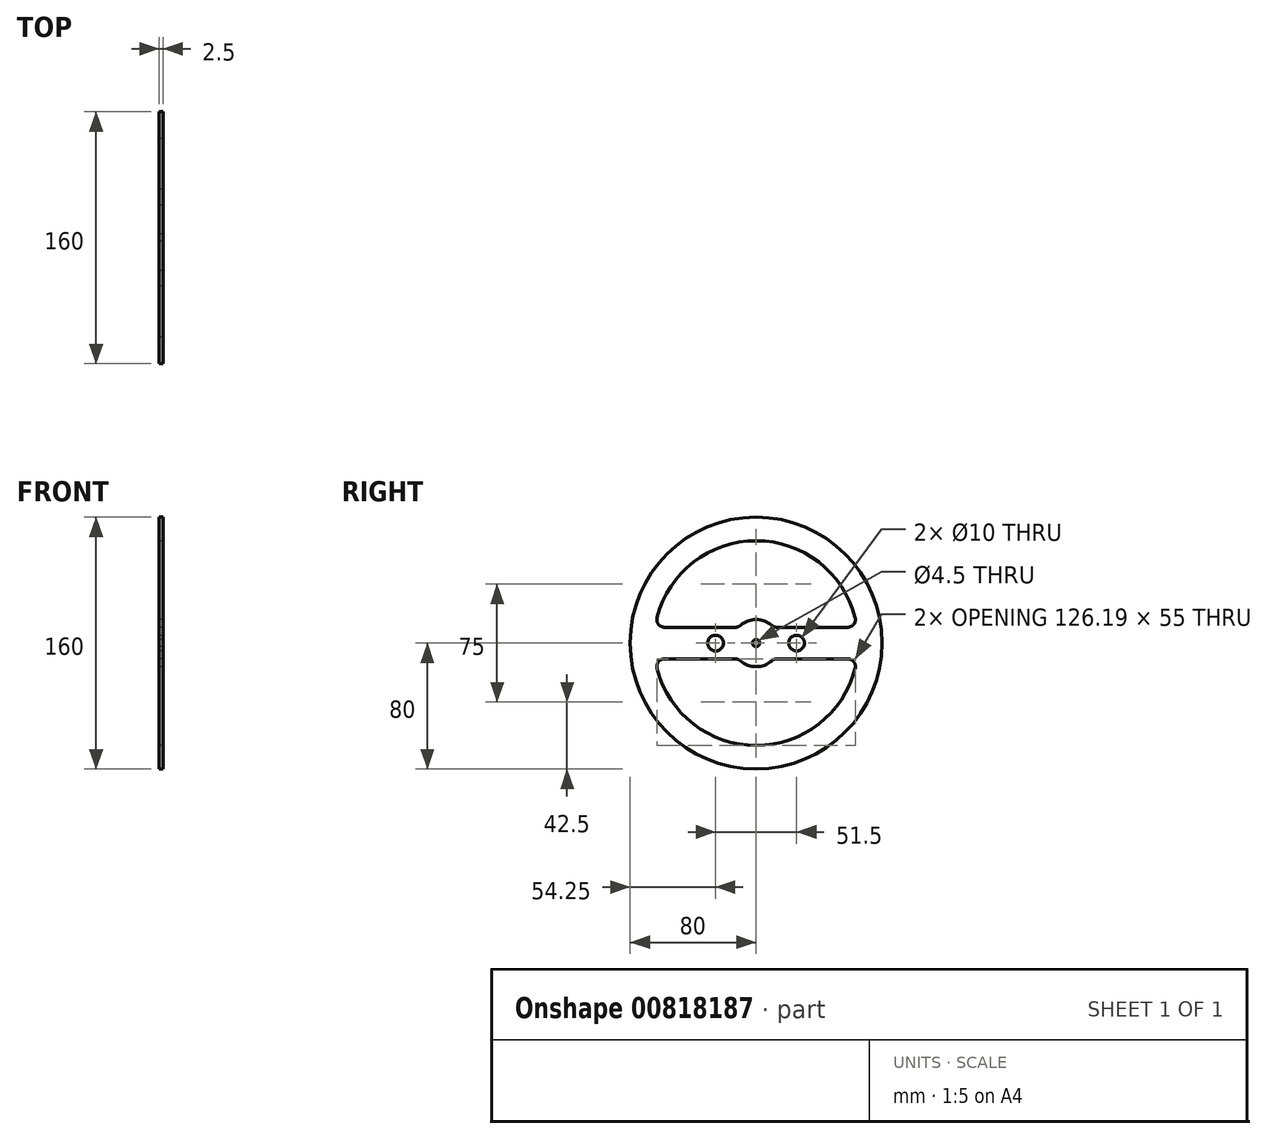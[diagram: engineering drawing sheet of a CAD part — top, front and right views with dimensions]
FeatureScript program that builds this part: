
annotation { "Feature Type Name" : "Feature", "Feature Type Description" : "" }
export const myFeature = defineFeature(function(context is Context, id is Id, definition is map)
    precondition{}
    {
        {
            var Q0;
            Q0=qCreatedBy(makeId("Right.planeOp"),FACE);
            var sketch = newSketch(context, id + "F0", { "sketchPlane" : qUnion([Q0])});
            skCircle(sketch, "E0", {"center": v(0, 0) * mm, "radius": 2.25 * mm});
            skCircle(sketch, "E1", {"center": v(25.75, 0) * mm, "radius": 5 * mm});
            skCircle(sketch, "E2", {"center": v(0, 0) * mm, "radius": 80 * mm});
            skCircle(sketch, "E3", {"center": v(0, 0) * mm, "radius": 15 * mm});
            skLineSegment(sketch, "E4", {"start": v(0, 0) * mm, "end": v(25.75, 0) * mm, "construction": true});
            skCircle(sketch, "E5", {"center": v(0, 0) * mm, "radius": 65 * mm});
            skLineSegment(sketch, "E6", {"start": v(0, 0) * mm, "end": v(0, 56.56) * mm, "construction": true});
            skLineSegment(sketch, "E7", {"start": v(64.23, 10) * mm, "end": v(11.18, 10) * mm});
            skLineSegment(sketch, "E8.MirrorCS", {"start": v(64.23, -10) * mm, "end": v(11.18, -10) * mm});
            skLineSegment(sketch, "E9.MirrorCS", {"start": v(-64.23, 10) * mm, "end": v(-11.18, 10) * mm});
            skCircle(sketch, "E10.MirrorC", {"center": v(-25.75, 0) * mm, "radius": 5 * mm});
            skLineSegment(sketch, "E11.MirrorCS", {"start": v(-64.23, -10) * mm, "end": v(-11.18, -10) * mm});
            skSolve(sketch);
        }
        {
            var Q0;
            Q0=makeQuery(id+"F0.imprint","IMPRINT",FACE,{"disambiguationData":[TD([[makeQuery(id+"F0.imprint","IMPRINT",EDGE,{"derivedFrom":sQuery(id+"F0.wireOp",EDGE,"E2")}),1.0]])]});
            var Q1;
            {var subQ0=sQuery(id+"F0.wireOp",EDGE,"E9.MirrorCS");Q1=makeQuery(id+"F0.imprint","IMPRINT",FACE,{"disambiguationData":[TD([[makeQuery(id+"F0.imprint","IMPRINT",EDGE,{"derivedFrom":subQ0}),-1.0]])]});}
            var Q2;
            Q2=makeQuery(id+"F0.imprint","IMPRINT",FACE,{"disambiguationData":[TD([[makeQuery(id+"F0.imprint","IMPRINT",EDGE,{"derivedFrom":sQuery(id+"F0.wireOp",EDGE,"E0")}),-1.0]])]});
            var Q3;
            {var subQ2=sQuery(id+"F0.wireOp",EDGE,"E1");Q3=makeQuery(id+"F0.imprint","IMPRINT",FACE,{"disambiguationData":[TD([[makeQuery(id+"F0.imprint","IMPRINT",EDGE,{"derivedFrom":subQ2}),-1.0]])]});}
            extrude(context, id + "F1", {"entities" : qUnion([Q0, Q1, Q2, Q3]), "depth" : 2.5 * mm, "offsetDistance" : 25 * mm});
        }
        {
            var Q0;
            Q0=makeQuery(id+"F1.opExtrude","SWEPT_EDGE",EDGE,{"disambiguationData":[OSD([sQuery(id+"F0.wireOp",EDGE,"E5"),sQuery(id+"F0.wireOp",EDGE,"E9.MirrorCS")])]});
            var Q1;
            Q1=makeQuery(id+"F1.opExtrude","SWEPT_EDGE",EDGE,{"disambiguationData":[OSD([sQuery(id+"F0.wireOp",EDGE,"E3"),sQuery(id+"F0.wireOp",EDGE,"E9.MirrorCS")])]});
            var Q2;
            Q2=makeQuery(id+"F1.opExtrude","SWEPT_EDGE",EDGE,{"disambiguationData":[OSD([sQuery(id+"F0.wireOp",EDGE,"E3"),sQuery(id+"F0.wireOp",EDGE,"E7")])]});
            var Q3;
            Q3=makeQuery(id+"F1.opExtrude","SWEPT_EDGE",EDGE,{"disambiguationData":[OSD([sQuery(id+"F0.wireOp",EDGE,"E5"),sQuery(id+"F0.wireOp",EDGE,"E7")])]});
            var Q4;
            Q4=makeQuery(id+"F1.opExtrude","SWEPT_EDGE",EDGE,{"disambiguationData":[OSD([sQuery(id+"F0.wireOp",EDGE,"E5"),sQuery(id+"F0.wireOp",EDGE,"E8.MirrorCS")])]});
            var Q5;
            Q5=makeQuery(id+"F1.opExtrude","SWEPT_EDGE",EDGE,{"disambiguationData":[OSD([sQuery(id+"F0.wireOp",EDGE,"E3"),sQuery(id+"F0.wireOp",EDGE,"E8.MirrorCS")])]});
            var Q6;
            Q6=makeQuery(id+"F1.opExtrude","SWEPT_EDGE",EDGE,{"disambiguationData":[OSD([sQuery(id+"F0.wireOp",EDGE,"E3"),sQuery(id+"F0.wireOp",EDGE,"E11.MirrorCS")])]});
            var Q7;
            Q7=makeQuery(id+"F1.opExtrude","SWEPT_EDGE",EDGE,{"disambiguationData":[OSD([sQuery(id+"F0.wireOp",EDGE,"E5"),sQuery(id+"F0.wireOp",EDGE,"E11.MirrorCS")])]});
            fillet(context, id + "F2", {"entities" : qUnion([Q0, Q1, Q2, Q3, Q4, Q5, Q6, Q7]), "radius" : 5 * mm, "tangentPropagation" : true, "allowEdgeOverflow" : false});
        }
    });
